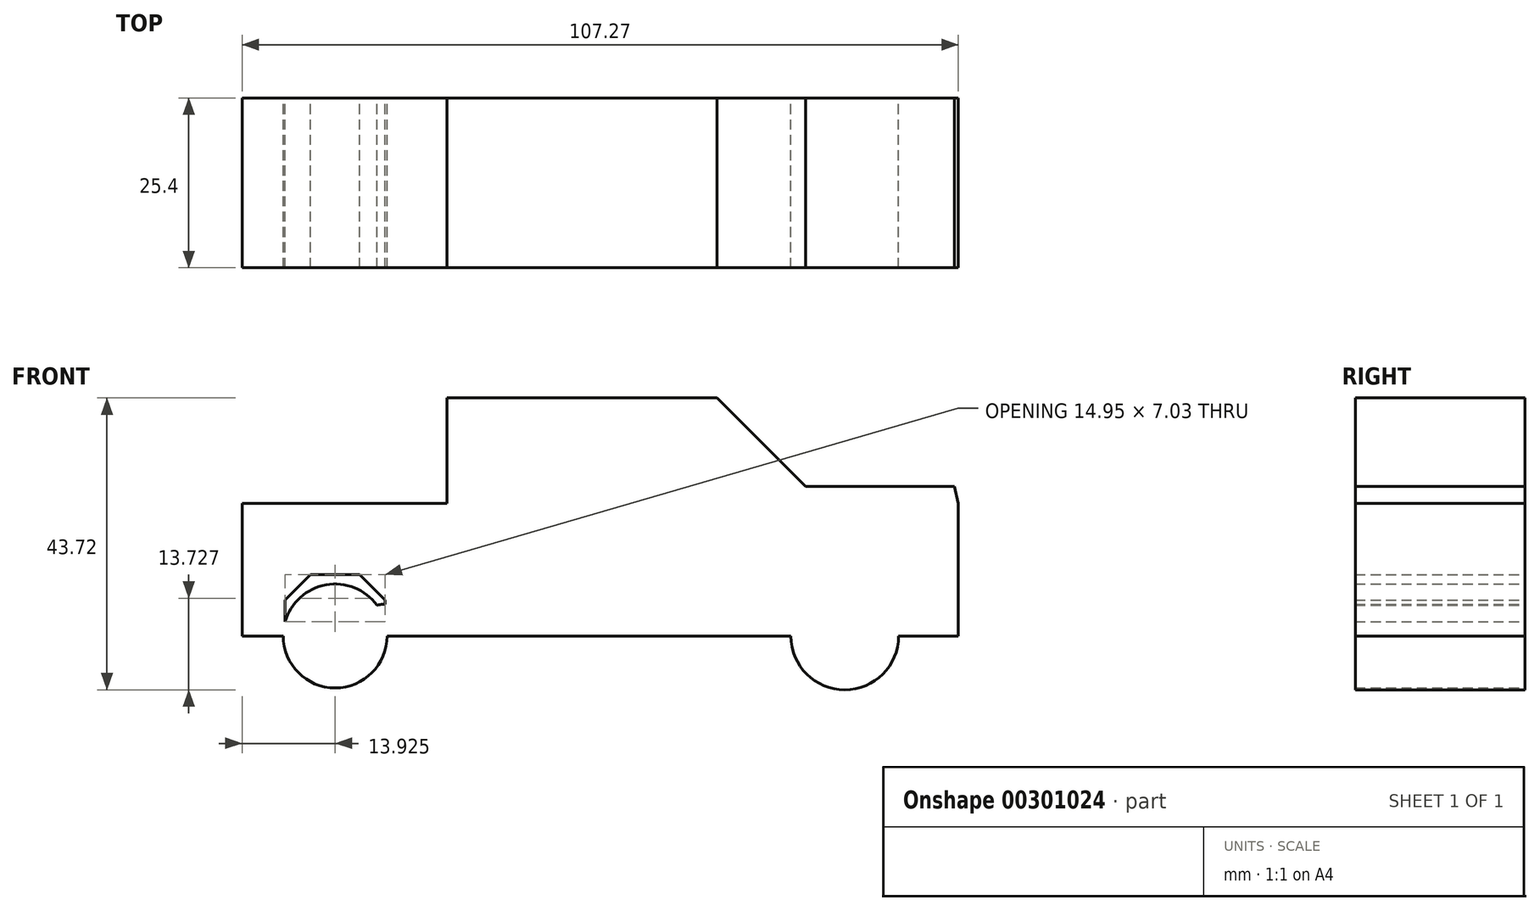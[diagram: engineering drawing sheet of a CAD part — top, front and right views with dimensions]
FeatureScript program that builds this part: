
annotation { "Feature Type Name" : "Feature", "Feature Type Description" : "" }
export const myFeature = defineFeature(function(context is Context, id is Id, definition is map)
    precondition{}
    {
        {
            var Q0;
            Q0=qCreatedBy(makeId("Front.planeOp"),FACE);
            var sketch = newSketch(context, id + "F0", { "sketchPlane" : qUnion([Q0])});
            skLineSegment(sketch, "E0", {"start": v(-59, 0) * mm, "end": v(-59, 19.83) * mm});
            skLineSegment(sketch, "E1", {"start": v(-59, 19.83) * mm, "end": v(-28.33, 19.83) * mm});
            skLineSegment(sketch, "E2", {"start": v(-28.33, 19.83) * mm, "end": v(-28.33, 35.66) * mm});
            skLineSegment(sketch, "E3", {"start": v(12.11, 35.66) * mm, "end": v(25.4, 22.37) * mm});
            skLineSegment(sketch, "E4", {"start": v(25.4, 22.37) * mm, "end": v(47.67, 22.37) * mm});
            skLineSegment(sketch, "E5", {"start": v(48.26, 19.83) * mm, "end": v(48.26, 16.9) * mm});
            skLineSegment(sketch, "E6", {"start": v(48.26, 19.83) * mm, "end": v(47.67, 22.37) * mm});
            skLineSegment(sketch, "E7", {"start": v(48.26, 16.9) * mm, "end": v(48.26, 0) * mm});
            skPoint(sketch, "E8.start.orphan", {"position": v(12.11, 22.37) * mm});
            skPoint(sketch, "E9.end.orphan", {"position": v(10.75, 35.66) * mm});
            skLineSegment(sketch, "E10", {"start": v(-28.33, 35.66) * mm, "end": v(12.11, 35.66) * mm});
            skLineSegment(sketch, "E11", {"start": v(-57.64, 0) * mm, "end": v(-52.56, 0) * mm});
            skLineSegment(sketch, "E12", {"start": v(-52.56, 0) * mm, "end": v(-52.56, 5.37) * mm});
            skLineSegment(sketch, "E13", {"start": v(-52.56, 5.37) * mm, "end": v(-48.75, 9.18) * mm});
            skLineSegment(sketch, "E14", {"start": v(-48.75, 9.18) * mm, "end": v(-41.42, 9.18) * mm});
            skLineSegment(sketch, "E15", {"start": v(-41.42, 9.18) * mm, "end": v(-37.61, 5.37) * mm});
            skLineSegment(sketch, "E16", {"start": v(-37.61, 5.37) * mm, "end": v(-37.61, 4.76) * mm});
            skLineSegment(sketch, "E17", {"start": v(23.45, 0) * mm, "end": v(23.45, 5.37) * mm});
            skLineSegment(sketch, "E18", {"start": v(23.45, 5.37) * mm, "end": v(27.26, 9.18) * mm});
            skLineSegment(sketch, "E19", {"start": v(27.26, 9.18) * mm, "end": v(34.78, 9.18) * mm});
            skLineSegment(sketch, "E20", {"start": v(34.97, 8.5) * mm, "end": v(38.1, 5.37) * mm});
            skLineSegment(sketch, "E21", {"start": v(38.1, 5.37) * mm, "end": v(38.1, 0) * mm});
            skCircle(sketch, "E22", {"center": v(-45.09, 0) * mm, "radius": 7.78 * mm});
            skPoint(sketch, "E22.centerSnap0", {"position": v(-45.09, 9.18) * mm});
            skCircle(sketch, "E23", {"center": v(31.26, 0) * mm, "radius": 8.06 * mm});
            skArc(sketch, "E24", {"start": v(-37.61, 4.76) * mm, "mid": v(-38.22, 4.72) * mm, "end": v(-38.82, 4.6) * mm});
            skLineSegment(sketch, "E25", {"start": v(-37.3, 0) * mm, "end": v(23.45, 0) * mm});
            skLineSegment(sketch, "E26", {"start": v(23.45, 0) * mm, "end": v(38.1, 0) * mm});
            skLineSegment(sketch, "E27", {"start": v(38.1, 0) * mm, "end": v(48.26, 0) * mm});
            skLineSegment(sketch, "E28", {"start": v(-57.64, 0) * mm, "end": v(-59, 0) * mm});
            skPoint(sketch, "E29.orphan", {"position": v(-51, 0) * mm});
            skSolve(sketch);
        }
        {
            var Q0;
            Q0 = qSketchRegion(id + "F0", true);
            var Q1;
            {var subQ0=sQuery(id+"F0.wireOp",EDGE,"E26");Q1=makeQuery(id+"F0.imprint","IMPRINT",FACE,{"disambiguationData":[TD([[makeQuery(id+"F0.imprint","IMPRINT",EDGE,{"derivedFrom":subQ0}),1.0]])]});}
            extrude(context, id + "F1", {"entities" : qUnion([Q0, Q1]), "depth" : 25.4 * mm});
        }
    });
